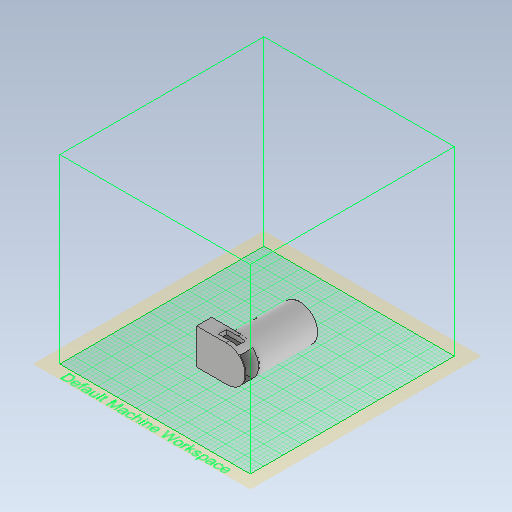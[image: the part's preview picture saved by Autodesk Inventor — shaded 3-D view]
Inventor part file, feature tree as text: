
AUTODESK INVENTOR PART (.ipt)
format: ipt  version: 2021 (Build 250183000, 183)  size: 401,408 bytes
history: native  units: in
note: dims shown in document units (in); Inventor stores cm internally (conversion verified against a paired STEP export)
features: sketch x15, extrude x11, plane x1
ambient origin geometry x8: Origin, YZ Plane, XZ Plane, XY Plane, X Axis, Y Axis, Z Axis, Center Point
bodies: Solid1 (feature_tree)
feature tree (27):
  extrude  "Extrusion1"  Depth=5.0in TaperAngle=0.0deg
  extrude  "Extrusion2"  Depth=5.0in TaperAngle=0.0deg
  extrude  "Extrusion3"  Depth=2.65in TaperAngle=0.0deg
  extrude  "Extrusion4"  Depth=1.1in
  plane  "Work Plane1"
  extrude  "Extrusion5"  Depth=1.175in
  extrude  "Extrusion6"  Depth=1.6in
  sketch  "Sketch7"  dims[d17=0.7in d18=4.0375in d19=0.0in]
  sketch  "Sketch8"  dims[d20=0.7in d21=0.9in]
  sketch  "Sketch9"  dims[d22=4.0375in d23=0.0in d24=2.3in]
  extrude  "Extrusion7"  Depth=0.7in TaperAngle=0.0deg
  extrude  "Extrusion8"  Depth=0.9in
  sketch  "Sketch12"  dims[d29=0.2in]
  extrude  "Extrusion9"  Depth=2.3in
  extrude  "Extrusion10"  Depth=1.0in
  extrude  "Extrusion11"  Depth=0.1in
  sketch  "Sketch1"  dims[d0=3.1in d1=5.0in d2=0.0in]
  sketch  "Sketch2"  dims[d3=3.0in d4=5.0in d5=0.0in]
  sketch  "Sketch3"  dims[d6=1.3in d7=0.0in d8=2.65in d9=0.0in]
  sketch  "Sketch4"  dims[d10=1.1in d11=1.15in]
  sketch  "Sketch5"  dims[d12=1.1in d13=1.175in]
  sketch  "Sketch6"  dims[d14=4.0875in d15=0.0in d16=1.6in]
  sketch  "Sketch10"  dims[d25=1.0in d26=1.0in]
  sketch  "Sketch11"  dims[d27=0.2in d28=0.1in]
  sketch  "Sketch13"  dims[d30=0.1in]
  sketch  "Sketch14"  dims[d31=0.2in]
  sketch  "Sketch15"  dims[d32=0.1in d33=3.275in d34=0.0in d35=3.1in d36=0.2in d37=0.0in d38=0.2in d39=0.0in d40=0.2in d41=2.325in d42=4.1in d43=0.0in]
